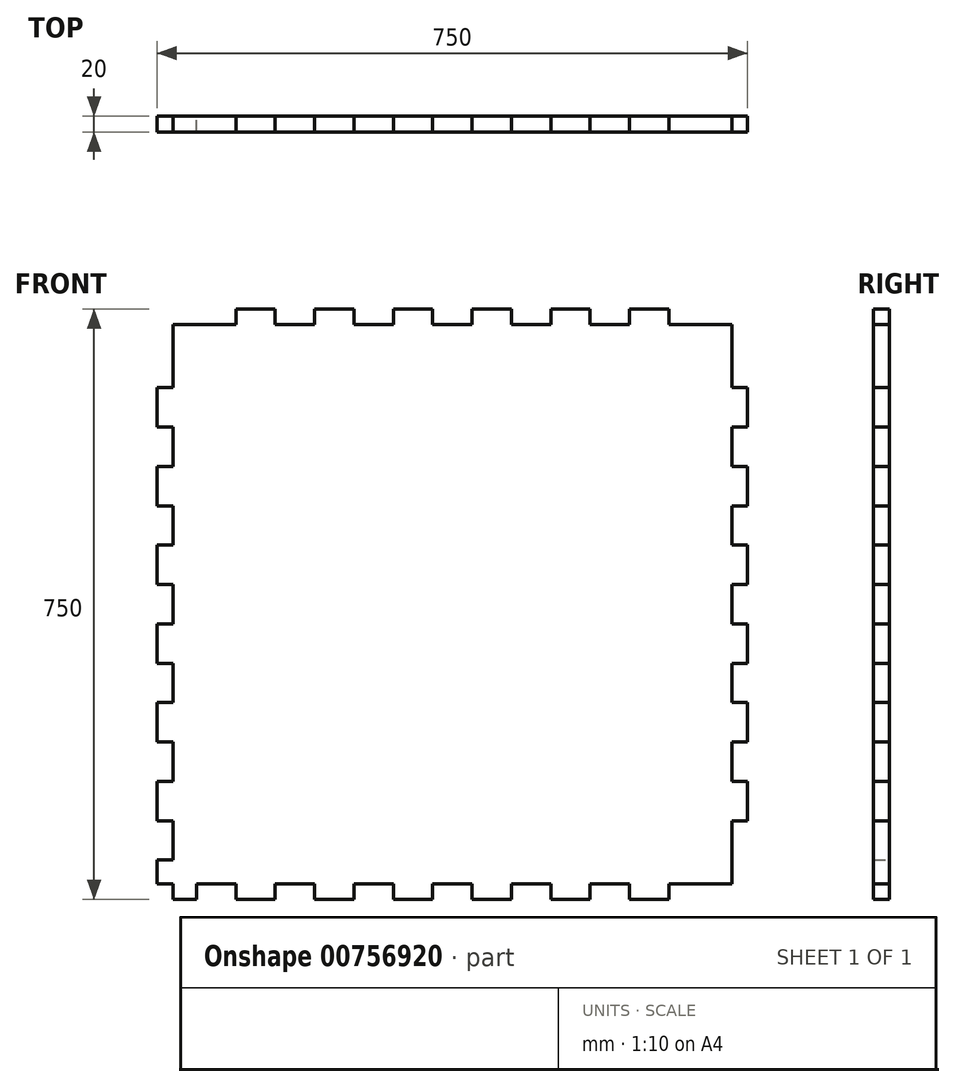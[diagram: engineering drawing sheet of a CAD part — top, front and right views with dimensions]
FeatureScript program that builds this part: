
annotation { "Feature Type Name" : "Feature", "Feature Type Description" : "" }
export const myFeature = defineFeature(function(context is Context, id is Id, definition is map)
    precondition{}
    {
        {
            var Q0;
            Q0=qCreatedBy(makeId("Front.planeOp"),FACE);
            var sketch = newSketch(context, id + "F0", { "sketchPlane" : qUnion([Q0])});
            skLineSegment(sketch, "E0.bottom", {"start": v(-346.83, 400) * mm, "end": v(403.17, 400) * mm});
            skLineSegment(sketch, "E0.top", {"start": v(-346.83, -350) * mm, "end": v(403.17, -350) * mm});
            skLineSegment(sketch, "E0.left", {"start": v(-346.83, 400) * mm, "end": v(-346.83, -350) * mm});
            skLineSegment(sketch, "E0.right", {"start": v(403.17, 400) * mm, "end": v(403.17, -350) * mm});
            skLineSegment(sketch, "E1.bottom", {"start": v(-346.83, 400) * mm, "end": v(-326.83, 400) * mm});
            skLineSegment(sketch, "E1.top", {"start": v(-346.83, 350) * mm, "end": v(-326.83, 350) * mm});
            skLineSegment(sketch, "E1.left", {"start": v(-346.83, 400) * mm, "end": v(-346.83, 350) * mm});
            skLineSegment(sketch, "E1.right", {"start": v(-326.83, 400) * mm, "end": v(-326.83, 350) * mm});
            skLineSegment(sketch, "E2.top", {"start": v(-346.83, 300) * mm, "end": v(-326.83, 300) * mm});
            skLineSegment(sketch, "E2.left", {"start": v(-346.83, 350) * mm, "end": v(-346.83, 300) * mm});
            skLineSegment(sketch, "E2.right", {"start": v(-326.83, 350) * mm, "end": v(-326.83, 300) * mm});
            skLineSegment(sketch, "E3.top", {"start": v(-346.83, 250) * mm, "end": v(-326.83, 250) * mm});
            skLineSegment(sketch, "E3.left", {"start": v(-346.83, 300) * mm, "end": v(-346.83, 250) * mm});
            skLineSegment(sketch, "E3.right", {"start": v(-326.83, 300) * mm, "end": v(-326.83, 250) * mm});
            skLineSegment(sketch, "E4.top", {"start": v(-346.83, 200) * mm, "end": v(-326.83, 200) * mm});
            skLineSegment(sketch, "E4.left", {"start": v(-346.83, 250) * mm, "end": v(-346.83, 200) * mm});
            skLineSegment(sketch, "E4.right", {"start": v(-326.83, 250) * mm, "end": v(-326.83, 200) * mm});
            skLineSegment(sketch, "E5.top", {"start": v(-346.83, 150) * mm, "end": v(-326.83, 150) * mm});
            skLineSegment(sketch, "E5.left", {"start": v(-346.83, 200) * mm, "end": v(-346.83, 150) * mm});
            skLineSegment(sketch, "E5.right", {"start": v(-326.83, 200) * mm, "end": v(-326.83, 150) * mm});
            skLineSegment(sketch, "E6.top", {"start": v(-346.83, 100) * mm, "end": v(-326.83, 100) * mm});
            skLineSegment(sketch, "E6.left", {"start": v(-346.83, 150) * mm, "end": v(-346.83, 100) * mm});
            skLineSegment(sketch, "E6.right", {"start": v(-326.83, 150) * mm, "end": v(-326.83, 100) * mm});
            skLineSegment(sketch, "E7.top", {"start": v(-346.83, 50) * mm, "end": v(-326.83, 50) * mm});
            skLineSegment(sketch, "E7.left", {"start": v(-346.83, 100) * mm, "end": v(-346.83, 50) * mm});
            skLineSegment(sketch, "E7.right", {"start": v(-326.83, 100) * mm, "end": v(-326.83, 50) * mm});
            skLineSegment(sketch, "E8.top", {"start": v(-346.83, 0) * mm, "end": v(-326.83, 0) * mm});
            skLineSegment(sketch, "E8.left", {"start": v(-346.83, 50) * mm, "end": v(-346.83, 0) * mm});
            skLineSegment(sketch, "E8.right", {"start": v(-326.83, 50) * mm, "end": v(-326.83, 0) * mm});
            skLineSegment(sketch, "E9.top", {"start": v(-346.83, -50) * mm, "end": v(-326.83, -50) * mm});
            skLineSegment(sketch, "E9.left", {"start": v(-346.83, 0) * mm, "end": v(-346.83, -50) * mm});
            skLineSegment(sketch, "E9.right", {"start": v(-326.83, 0) * mm, "end": v(-326.83, -50) * mm});
            skLineSegment(sketch, "E10.top", {"start": v(-346.83, -100) * mm, "end": v(-326.83, -100) * mm});
            skLineSegment(sketch, "E10.left", {"start": v(-346.83, -50) * mm, "end": v(-346.83, -100) * mm});
            skLineSegment(sketch, "E10.right", {"start": v(-326.83, -50) * mm, "end": v(-326.83, -100) * mm});
            skLineSegment(sketch, "E11.top", {"start": v(-346.83, -150) * mm, "end": v(-326.83, -150) * mm});
            skLineSegment(sketch, "E11.left", {"start": v(-346.83, -100) * mm, "end": v(-346.83, -150) * mm});
            skLineSegment(sketch, "E11.right", {"start": v(-326.83, -100) * mm, "end": v(-326.83, -150) * mm});
            skLineSegment(sketch, "E12.top", {"start": v(-346.83, -200) * mm, "end": v(-326.83, -200) * mm});
            skLineSegment(sketch, "E12.left", {"start": v(-346.83, -150) * mm, "end": v(-346.83, -200) * mm});
            skLineSegment(sketch, "E12.right", {"start": v(-326.83, -150) * mm, "end": v(-326.83, -200) * mm});
            skLineSegment(sketch, "E13.top", {"start": v(-346.83, -250) * mm, "end": v(-326.83, -250) * mm});
            skLineSegment(sketch, "E13.left", {"start": v(-346.83, -200) * mm, "end": v(-346.83, -250) * mm});
            skLineSegment(sketch, "E13.right", {"start": v(-326.83, -200) * mm, "end": v(-326.83, -250) * mm});
            skLineSegment(sketch, "E14.top", {"start": v(-346.83, -300) * mm, "end": v(-326.83, -300) * mm});
            skLineSegment(sketch, "E14.left", {"start": v(-346.83, -250) * mm, "end": v(-346.83, -300) * mm});
            skLineSegment(sketch, "E14.right", {"start": v(-326.83, -250) * mm, "end": v(-326.83, -300) * mm});
            skLineSegment(sketch, "E15.top", {"start": v(-346.83, -350) * mm, "end": v(-326.83, -350) * mm});
            skLineSegment(sketch, "E15.left", {"start": v(-346.83, -300) * mm, "end": v(-346.83, -350) * mm});
            skLineSegment(sketch, "E15.right", {"start": v(-326.83, -300) * mm, "end": v(-326.83, -350) * mm});
            skLineSegment(sketch, "E16.bottom", {"start": v(-346.83, -350) * mm, "end": v(-296.83, -350) * mm});
            skLineSegment(sketch, "E16.top", {"start": v(-346.83, -330) * mm, "end": v(-296.83, -330) * mm});
            skLineSegment(sketch, "E16.left", {"start": v(-346.83, -350) * mm, "end": v(-346.83, -330) * mm});
            skLineSegment(sketch, "E16.right", {"start": v(-296.83, -350) * mm, "end": v(-296.83, -330) * mm});
            skLineSegment(sketch, "E17.bottom", {"start": v(-296.83, -350) * mm, "end": v(-246.83, -350) * mm});
            skLineSegment(sketch, "E17.top", {"start": v(-296.83, -330) * mm, "end": v(-246.83, -330) * mm});
            skLineSegment(sketch, "E17.right", {"start": v(-246.83, -350) * mm, "end": v(-246.83, -330) * mm});
            skLineSegment(sketch, "E18.bottom", {"start": v(-246.83, -330) * mm, "end": v(-196.83, -330) * mm});
            skLineSegment(sketch, "E18.top", {"start": v(-246.83, -350) * mm, "end": v(-196.83, -350) * mm});
            skLineSegment(sketch, "E18.left", {"start": v(-246.83, -330) * mm, "end": v(-246.83, -350) * mm});
            skLineSegment(sketch, "E18.right", {"start": v(-196.83, -330) * mm, "end": v(-196.83, -350) * mm});
            skLineSegment(sketch, "E19.bottom", {"start": v(-196.83, -330) * mm, "end": v(-146.83, -330) * mm});
            skLineSegment(sketch, "E19.top", {"start": v(-196.83, -350) * mm, "end": v(-146.83, -350) * mm});
            skLineSegment(sketch, "E19.right", {"start": v(-146.83, -330) * mm, "end": v(-146.83, -350) * mm});
            skLineSegment(sketch, "E20.bottom", {"start": v(-146.83, -330) * mm, "end": v(-96.83, -330) * mm});
            skLineSegment(sketch, "E20.top", {"start": v(-146.83, -350) * mm, "end": v(-96.83, -350) * mm});
            skLineSegment(sketch, "E20.right", {"start": v(-96.83, -330) * mm, "end": v(-96.83, -350) * mm});
            skLineSegment(sketch, "E21.bottom", {"start": v(-96.83, -330) * mm, "end": v(-46.83, -330) * mm});
            skLineSegment(sketch, "E21.top", {"start": v(-96.83, -350) * mm, "end": v(-46.83, -350) * mm});
            skLineSegment(sketch, "E21.right", {"start": v(-46.83, -330) * mm, "end": v(-46.83, -350) * mm});
            skLineSegment(sketch, "E22.bottom", {"start": v(-46.83, -330) * mm, "end": v(3.17, -330) * mm});
            skLineSegment(sketch, "E22.top", {"start": v(-46.83, -350) * mm, "end": v(3.17, -350) * mm});
            skLineSegment(sketch, "E22.right", {"start": v(3.17, -330) * mm, "end": v(3.17, -350) * mm});
            skLineSegment(sketch, "E23.bottom", {"start": v(3.17, -330) * mm, "end": v(53.17, -330) * mm});
            skLineSegment(sketch, "E23.top", {"start": v(3.17, -350) * mm, "end": v(53.17, -350) * mm});
            skLineSegment(sketch, "E23.right", {"start": v(53.17, -330) * mm, "end": v(53.17, -350) * mm});
            skLineSegment(sketch, "E24.bottom", {"start": v(53.17, -330) * mm, "end": v(103.17, -330) * mm});
            skLineSegment(sketch, "E24.top", {"start": v(53.17, -350) * mm, "end": v(103.17, -350) * mm});
            skLineSegment(sketch, "E24.right", {"start": v(103.17, -330) * mm, "end": v(103.17, -350) * mm});
            skLineSegment(sketch, "E25.bottom", {"start": v(103.17, -330) * mm, "end": v(153.17, -330) * mm});
            skLineSegment(sketch, "E25.top", {"start": v(103.17, -350) * mm, "end": v(153.17, -350) * mm});
            skLineSegment(sketch, "E25.right", {"start": v(153.17, -330) * mm, "end": v(153.17, -350) * mm});
            skLineSegment(sketch, "E26.bottom", {"start": v(153.17, -330) * mm, "end": v(203.17, -330) * mm});
            skLineSegment(sketch, "E26.top", {"start": v(153.17, -350) * mm, "end": v(203.17, -350) * mm});
            skLineSegment(sketch, "E26.right", {"start": v(203.17, -330) * mm, "end": v(203.17, -350) * mm});
            skLineSegment(sketch, "E27.bottom", {"start": v(203.17, -330) * mm, "end": v(253.17, -330) * mm});
            skLineSegment(sketch, "E27.top", {"start": v(203.17, -350) * mm, "end": v(253.17, -350) * mm});
            skLineSegment(sketch, "E27.right", {"start": v(253.17, -330) * mm, "end": v(253.17, -350) * mm});
            skLineSegment(sketch, "E28.bottom", {"start": v(253.17, -330) * mm, "end": v(303.17, -330) * mm});
            skLineSegment(sketch, "E28.top", {"start": v(253.17, -350) * mm, "end": v(303.17, -350) * mm});
            skLineSegment(sketch, "E28.right", {"start": v(303.17, -330) * mm, "end": v(303.17, -350) * mm});
            skLineSegment(sketch, "E29.bottom", {"start": v(303.17, -330) * mm, "end": v(353.17, -330) * mm});
            skLineSegment(sketch, "E29.top", {"start": v(303.17, -350) * mm, "end": v(353.17, -350) * mm});
            skLineSegment(sketch, "E29.right", {"start": v(353.17, -330) * mm, "end": v(353.17, -350) * mm});
            skLineSegment(sketch, "E30.bottom", {"start": v(353.17, -330) * mm, "end": v(403.17, -330) * mm});
            skLineSegment(sketch, "E30.top", {"start": v(353.17, -350) * mm, "end": v(403.17, -350) * mm});
            skLineSegment(sketch, "E30.right", {"start": v(403.17, -330) * mm, "end": v(403.17, -350) * mm});
            skLineSegment(sketch, "E31.bottom", {"start": v(-346.83, 400) * mm, "end": v(-296.83, 400) * mm});
            skLineSegment(sketch, "E31.top", {"start": v(-346.83, 380) * mm, "end": v(-296.83, 380) * mm});
            skLineSegment(sketch, "E31.left", {"start": v(-346.83, 400) * mm, "end": v(-346.83, 380) * mm});
            skLineSegment(sketch, "E31.right", {"start": v(-296.83, 400) * mm, "end": v(-296.83, 380) * mm});
            skLineSegment(sketch, "E32.bottom", {"start": v(-296.83, 380) * mm, "end": v(-246.83, 380) * mm});
            skLineSegment(sketch, "E32.top", {"start": v(-296.83, 400) * mm, "end": v(-246.83, 400) * mm});
            skLineSegment(sketch, "E32.left", {"start": v(-296.83, 380) * mm, "end": v(-296.83, 400) * mm});
            skLineSegment(sketch, "E32.right", {"start": v(-246.83, 380) * mm, "end": v(-246.83, 400) * mm});
            skLineSegment(sketch, "E33.bottom", {"start": v(-246.83, 380) * mm, "end": v(-196.83, 380) * mm});
            skLineSegment(sketch, "E33.top", {"start": v(-246.83, 400) * mm, "end": v(-196.83, 400) * mm});
            skLineSegment(sketch, "E33.right", {"start": v(-196.83, 380) * mm, "end": v(-196.83, 400) * mm});
            skLineSegment(sketch, "E34.bottom", {"start": v(-196.83, 380) * mm, "end": v(-146.83, 380) * mm});
            skLineSegment(sketch, "E34.top", {"start": v(-196.83, 400) * mm, "end": v(-146.83, 400) * mm});
            skLineSegment(sketch, "E34.right", {"start": v(-146.83, 380) * mm, "end": v(-146.83, 400) * mm});
            skLineSegment(sketch, "E35.bottom", {"start": v(-146.83, 380) * mm, "end": v(-96.83, 380) * mm});
            skLineSegment(sketch, "E35.top", {"start": v(-146.83, 400) * mm, "end": v(-96.83, 400) * mm});
            skLineSegment(sketch, "E35.right", {"start": v(-96.83, 380) * mm, "end": v(-96.83, 400) * mm});
            skLineSegment(sketch, "E36.bottom", {"start": v(-96.83, 380) * mm, "end": v(-46.83, 380) * mm});
            skLineSegment(sketch, "E36.top", {"start": v(-96.83, 400) * mm, "end": v(-46.83, 400) * mm});
            skLineSegment(sketch, "E36.right", {"start": v(-46.83, 380) * mm, "end": v(-46.83, 400) * mm});
            skLineSegment(sketch, "E37.bottom", {"start": v(-46.83, 380) * mm, "end": v(3.17, 380) * mm});
            skLineSegment(sketch, "E37.top", {"start": v(-46.83, 400) * mm, "end": v(3.17, 400) * mm});
            skLineSegment(sketch, "E37.right", {"start": v(3.17, 380) * mm, "end": v(3.17, 400) * mm});
            skLineSegment(sketch, "E38.bottom", {"start": v(3.17, 380) * mm, "end": v(53.17, 380) * mm});
            skLineSegment(sketch, "E38.top", {"start": v(3.17, 400) * mm, "end": v(53.17, 400) * mm});
            skLineSegment(sketch, "E38.right", {"start": v(53.17, 380) * mm, "end": v(53.17, 400) * mm});
            skLineSegment(sketch, "E39.bottom", {"start": v(53.17, 380) * mm, "end": v(103.17, 380) * mm});
            skLineSegment(sketch, "E39.top", {"start": v(53.17, 400) * mm, "end": v(103.17, 400) * mm});
            skLineSegment(sketch, "E39.right", {"start": v(103.17, 380) * mm, "end": v(103.17, 400) * mm});
            skLineSegment(sketch, "E40.bottom", {"start": v(103.17, 380) * mm, "end": v(153.17, 380) * mm});
            skLineSegment(sketch, "E40.top", {"start": v(103.17, 400) * mm, "end": v(153.17, 400) * mm});
            skLineSegment(sketch, "E40.right", {"start": v(153.17, 380) * mm, "end": v(153.17, 400) * mm});
            skLineSegment(sketch, "E41.bottom", {"start": v(153.17, 380) * mm, "end": v(203.17, 380) * mm});
            skLineSegment(sketch, "E41.top", {"start": v(153.17, 400) * mm, "end": v(203.17, 400) * mm});
            skLineSegment(sketch, "E41.right", {"start": v(203.17, 380) * mm, "end": v(203.17, 400) * mm});
            skLineSegment(sketch, "E42.bottom", {"start": v(203.17, 380) * mm, "end": v(253.17, 380) * mm});
            skLineSegment(sketch, "E42.top", {"start": v(203.17, 400) * mm, "end": v(253.17, 400) * mm});
            skLineSegment(sketch, "E42.right", {"start": v(253.17, 380) * mm, "end": v(253.17, 400) * mm});
            skLineSegment(sketch, "E43.bottom", {"start": v(253.17, 380) * mm, "end": v(303.17, 380) * mm});
            skLineSegment(sketch, "E43.top", {"start": v(253.17, 400) * mm, "end": v(303.17, 400) * mm});
            skLineSegment(sketch, "E43.right", {"start": v(303.17, 380) * mm, "end": v(303.17, 400) * mm});
            skLineSegment(sketch, "E44.bottom", {"start": v(303.17, 380) * mm, "end": v(353.17, 380) * mm});
            skLineSegment(sketch, "E44.top", {"start": v(303.17, 400) * mm, "end": v(353.17, 400) * mm});
            skLineSegment(sketch, "E44.right", {"start": v(353.17, 380) * mm, "end": v(353.17, 400) * mm});
            skLineSegment(sketch, "E45.bottom", {"start": v(353.17, 380) * mm, "end": v(403.17, 380) * mm});
            skLineSegment(sketch, "E45.top", {"start": v(353.17, 400) * mm, "end": v(403.17, 400) * mm});
            skLineSegment(sketch, "E45.right", {"start": v(403.17, 380) * mm, "end": v(403.17, 400) * mm});
            skLineSegment(sketch, "E46.bottom", {"start": v(403.17, 400) * mm, "end": v(383.17, 400) * mm});
            skLineSegment(sketch, "E46.top", {"start": v(403.17, 350) * mm, "end": v(383.17, 350) * mm});
            skLineSegment(sketch, "E46.left", {"start": v(403.17, 400) * mm, "end": v(403.17, 350) * mm});
            skLineSegment(sketch, "E46.right", {"start": v(383.17, 400) * mm, "end": v(383.17, 350) * mm});
            skLineSegment(sketch, "E47.bottom", {"start": v(383.17, 350) * mm, "end": v(403.17, 350) * mm});
            skLineSegment(sketch, "E47.top", {"start": v(383.17, 300) * mm, "end": v(403.17, 300) * mm});
            skLineSegment(sketch, "E47.left", {"start": v(383.17, 350) * mm, "end": v(383.17, 300) * mm});
            skLineSegment(sketch, "E47.right", {"start": v(403.17, 350) * mm, "end": v(403.17, 300) * mm});
            skLineSegment(sketch, "E48.top", {"start": v(383.17, 250) * mm, "end": v(403.17, 250) * mm});
            skLineSegment(sketch, "E48.left", {"start": v(383.17, 300) * mm, "end": v(383.17, 250) * mm});
            skLineSegment(sketch, "E48.right", {"start": v(403.17, 300) * mm, "end": v(403.17, 250) * mm});
            skLineSegment(sketch, "E49.top", {"start": v(383.17, 200) * mm, "end": v(403.17, 200) * mm});
            skLineSegment(sketch, "E49.left", {"start": v(383.17, 250) * mm, "end": v(383.17, 200) * mm});
            skLineSegment(sketch, "E49.right", {"start": v(403.17, 250) * mm, "end": v(403.17, 200) * mm});
            skLineSegment(sketch, "E50.top", {"start": v(383.17, 150) * mm, "end": v(403.17, 150) * mm});
            skLineSegment(sketch, "E50.left", {"start": v(383.17, 200) * mm, "end": v(383.17, 150) * mm});
            skLineSegment(sketch, "E50.right", {"start": v(403.17, 200) * mm, "end": v(403.17, 150) * mm});
            skLineSegment(sketch, "E51.top", {"start": v(383.17, 100) * mm, "end": v(403.17, 100) * mm});
            skLineSegment(sketch, "E51.left", {"start": v(383.17, 150) * mm, "end": v(383.17, 100) * mm});
            skLineSegment(sketch, "E51.right", {"start": v(403.17, 150) * mm, "end": v(403.17, 100) * mm});
            skLineSegment(sketch, "E52.top", {"start": v(383.17, 50) * mm, "end": v(403.17, 50) * mm});
            skLineSegment(sketch, "E52.left", {"start": v(383.17, 100) * mm, "end": v(383.17, 50) * mm});
            skLineSegment(sketch, "E52.right", {"start": v(403.17, 100) * mm, "end": v(403.17, 50) * mm});
            skLineSegment(sketch, "E53.top", {"start": v(383.17, 0) * mm, "end": v(403.17, 0) * mm});
            skLineSegment(sketch, "E53.left", {"start": v(383.17, 50) * mm, "end": v(383.17, 0) * mm});
            skLineSegment(sketch, "E53.right", {"start": v(403.17, 50) * mm, "end": v(403.17, 0) * mm});
            skLineSegment(sketch, "E54.top", {"start": v(383.17, -50) * mm, "end": v(403.17, -50) * mm});
            skLineSegment(sketch, "E54.left", {"start": v(383.17, 0) * mm, "end": v(383.17, -50) * mm});
            skLineSegment(sketch, "E54.right", {"start": v(403.17, 0) * mm, "end": v(403.17, -50) * mm});
            skLineSegment(sketch, "E55.top", {"start": v(383.17, -100) * mm, "end": v(403.17, -100) * mm});
            skLineSegment(sketch, "E55.left", {"start": v(383.17, -50) * mm, "end": v(383.17, -100) * mm});
            skLineSegment(sketch, "E55.right", {"start": v(403.17, -50) * mm, "end": v(403.17, -100) * mm});
            skLineSegment(sketch, "E56.top", {"start": v(383.17, -150) * mm, "end": v(403.17, -150) * mm});
            skLineSegment(sketch, "E56.left", {"start": v(383.17, -100) * mm, "end": v(383.17, -150) * mm});
            skLineSegment(sketch, "E56.right", {"start": v(403.17, -100) * mm, "end": v(403.17, -150) * mm});
            skLineSegment(sketch, "E57.top", {"start": v(383.17, -200) * mm, "end": v(403.17, -200) * mm});
            skLineSegment(sketch, "E57.left", {"start": v(383.17, -150) * mm, "end": v(383.17, -200) * mm});
            skLineSegment(sketch, "E57.right", {"start": v(403.17, -150) * mm, "end": v(403.17, -200) * mm});
            skLineSegment(sketch, "E58.top", {"start": v(383.17, -250) * mm, "end": v(403.17, -250) * mm});
            skLineSegment(sketch, "E58.left", {"start": v(383.17, -200) * mm, "end": v(383.17, -250) * mm});
            skLineSegment(sketch, "E58.right", {"start": v(403.17, -200) * mm, "end": v(403.17, -250) * mm});
            skLineSegment(sketch, "E59.top", {"start": v(383.17, -300) * mm, "end": v(403.17, -300) * mm});
            skLineSegment(sketch, "E59.left", {"start": v(383.17, -250) * mm, "end": v(383.17, -300) * mm});
            skLineSegment(sketch, "E59.right", {"start": v(403.17, -250) * mm, "end": v(403.17, -300) * mm});
            skLineSegment(sketch, "E60.top", {"start": v(383.17, -350) * mm, "end": v(403.17, -350) * mm});
            skLineSegment(sketch, "E60.left", {"start": v(383.17, -300) * mm, "end": v(383.17, -350) * mm});
            skLineSegment(sketch, "E60.right", {"start": v(403.17, -300) * mm, "end": v(403.17, -350) * mm});
            skSolve(sketch);
        }
        {
            var Q0;
            {var subQ5=sQuery(id+"F0.wireOp",EDGE,"E31.left");Q0=makeQuery(id+"F0.imprint","IMPRINT",FACE,{"disambiguationData":[TD([[makeQuery(id+"F0.imprint","IMPRINT",EDGE,{"derivedFrom":subQ5}),1.0]])]});}
            var Q1;
            {var subQ0=sQuery(id+"F0.wireOp",EDGE,"E1.left");Q1=makeQuery(id+"F0.imprint","IMPRINT",FACE,{"disambiguationData":[TD([[makeQuery(id+"F0.imprint","IMPRINT",EDGE,{"derivedFrom":subQ0}),1.0]])]});}
            var Q2;
            {var subQ5=sQuery(id+"F0.wireOp",EDGE,"E32.left");Q2=makeQuery(id+"F0.imprint","IMPRINT",FACE,{"disambiguationData":[TD([[makeQuery(id+"F0.imprint","IMPRINT",EDGE,{"derivedFrom":subQ5}),1.0]])]});}
            var Q3;
            Q3=makeQuery(id+"F0.imprint","IMPRINT",FACE,{"disambiguationData":[TD([[makeQuery(id+"F0.imprint","IMPRINT",EDGE,{"derivedFrom":sQuery(id+"F0.wireOp",EDGE,"E33.bottom")}),1.0]])]});
            var Q4;
            Q4=makeQuery(id+"F0.imprint","IMPRINT",FACE,{"disambiguationData":[TD([[makeQuery(id+"F0.imprint","IMPRINT",EDGE,{"derivedFrom":sQuery(id+"F0.wireOp",EDGE,"E35.bottom")}),1.0]])]});
            var Q5;
            Q5=makeQuery(id+"F0.imprint","IMPRINT",FACE,{"disambiguationData":[TD([[makeQuery(id+"F0.imprint","IMPRINT",EDGE,{"derivedFrom":sQuery(id+"F0.wireOp",EDGE,"E37.bottom")}),1.0]])]});
            var Q6;
            Q6=makeQuery(id+"F0.imprint","IMPRINT",FACE,{"disambiguationData":[TD([[makeQuery(id+"F0.imprint","IMPRINT",EDGE,{"derivedFrom":sQuery(id+"F0.wireOp",EDGE,"E39.bottom")}),1.0]])]});
            var Q7;
            Q7=makeQuery(id+"F0.imprint","IMPRINT",FACE,{"disambiguationData":[TD([[makeQuery(id+"F0.imprint","IMPRINT",EDGE,{"derivedFrom":sQuery(id+"F0.wireOp",EDGE,"E41.bottom")}),1.0]])]});
            var Q8;
            Q8=makeQuery(id+"F0.imprint","IMPRINT",FACE,{"disambiguationData":[TD([[makeQuery(id+"F0.imprint","IMPRINT",EDGE,{"derivedFrom":sQuery(id+"F0.wireOp",EDGE,"E43.bottom")}),1.0]])]});
            var Q9;
            {var subQ4=sQuery(id+"F0.wireOp",EDGE,"E45.top");Q9=makeQuery(id+"F0.imprint","IMPRINT",FACE,{"disambiguationData":[TD([[makeQuery(id+"F0.imprint","IMPRINT",EDGE,{"derivedFrom":subQ4}),-1.0]])]});}
            var Q10;
            {var subQ5=sQuery(id+"F0.wireOp",EDGE,"E46.bottom");Q10=makeQuery(id+"F0.imprint","IMPRINT",FACE,{"disambiguationData":[TD([[makeQuery(id+"F0.imprint","IMPRINT",EDGE,{"derivedFrom":subQ5}),1.0]])]});}
            var Q11;
            {var subQ5=sQuery(id+"F0.wireOp",EDGE,"E47.bottom");Q11=makeQuery(id+"F0.imprint","IMPRINT",FACE,{"disambiguationData":[TD([[makeQuery(id+"F0.imprint","IMPRINT",EDGE,{"derivedFrom":subQ5}),1.0]])]});}
            var Q12;
            Q12=makeQuery(id+"F0.imprint","IMPRINT",FACE,{"disambiguationData":[TD([[makeQuery(id+"F0.imprint","IMPRINT",EDGE,{"derivedFrom":sQuery(id+"F0.wireOp",EDGE,"E2.top")}),-1.0]])]});
            var Q13;
            Q13=makeQuery(id+"F0.imprint","IMPRINT",FACE,{"disambiguationData":[TD([[makeQuery(id+"F0.imprint","IMPRINT",EDGE,{"derivedFrom":sQuery(id+"F0.wireOp",EDGE,"E4.top")}),-1.0]])]});
            var Q14;
            Q14=makeQuery(id+"F0.imprint","IMPRINT",FACE,{"disambiguationData":[TD([[makeQuery(id+"F0.imprint","IMPRINT",EDGE,{"derivedFrom":sQuery(id+"F0.wireOp",EDGE,"E6.top")}),-1.0]])]});
            var Q15;
            Q15=makeQuery(id+"F0.imprint","IMPRINT",FACE,{"disambiguationData":[TD([[makeQuery(id+"F0.imprint","IMPRINT",EDGE,{"derivedFrom":sQuery(id+"F0.wireOp",EDGE,"E8.top")}),-1.0]])]});
            var Q16;
            Q16=makeQuery(id+"F0.imprint","IMPRINT",FACE,{"disambiguationData":[TD([[makeQuery(id+"F0.imprint","IMPRINT",EDGE,{"derivedFrom":sQuery(id+"F0.wireOp",EDGE,"E10.top")}),-1.0]])]});
            var Q17;
            Q17=makeQuery(id+"F0.imprint","IMPRINT",FACE,{"disambiguationData":[TD([[makeQuery(id+"F0.imprint","IMPRINT",EDGE,{"derivedFrom":sQuery(id+"F0.wireOp",EDGE,"E12.top")}),-1.0]])]});
            var Q18;
            {var subQ0=sQuery(id+"F0.wireOp",EDGE,"E14.top");Q18=makeQuery(id+"F0.imprint","IMPRINT",FACE,{"disambiguationData":[TD([[makeQuery(id+"F0.imprint","IMPRINT",EDGE,{"derivedFrom":subQ0}),-1.0]])]});}
            var Q19;
            {var subQ5=sQuery(id+"F0.wireOp",EDGE,"E16.left");Q19=makeQuery(id+"F0.imprint","IMPRINT",FACE,{"disambiguationData":[TD([[makeQuery(id+"F0.imprint","IMPRINT",EDGE,{"derivedFrom":subQ5}),-1.0]])]});}
            var Q20;
            {var subQ5=sQuery(id+"F0.wireOp",EDGE,"E16.right");Q20=makeQuery(id+"F0.imprint","IMPRINT",FACE,{"disambiguationData":[TD([[makeQuery(id+"F0.imprint","IMPRINT",EDGE,{"derivedFrom":subQ5}),1.0]])]});}
            var Q21;
            Q21=makeQuery(id+"F0.imprint","IMPRINT",FACE,{"disambiguationData":[TD([[makeQuery(id+"F0.imprint","IMPRINT",EDGE,{"derivedFrom":sQuery(id+"F0.wireOp",EDGE,"E18.bottom")}),-1.0]])]});
            var Q22;
            Q22=makeQuery(id+"F0.imprint","IMPRINT",FACE,{"disambiguationData":[TD([[makeQuery(id+"F0.imprint","IMPRINT",EDGE,{"derivedFrom":sQuery(id+"F0.wireOp",EDGE,"E20.bottom")}),-1.0]])]});
            var Q23;
            Q23=makeQuery(id+"F0.imprint","IMPRINT",FACE,{"disambiguationData":[TD([[makeQuery(id+"F0.imprint","IMPRINT",EDGE,{"derivedFrom":sQuery(id+"F0.wireOp",EDGE,"E22.bottom")}),-1.0]])]});
            var Q24;
            Q24=makeQuery(id+"F0.imprint","IMPRINT",FACE,{"disambiguationData":[TD([[makeQuery(id+"F0.imprint","IMPRINT",EDGE,{"derivedFrom":sQuery(id+"F0.wireOp",EDGE,"E24.bottom")}),-1.0]])]});
            var Q25;
            Q25=makeQuery(id+"F0.imprint","IMPRINT",FACE,{"disambiguationData":[TD([[makeQuery(id+"F0.imprint","IMPRINT",EDGE,{"derivedFrom":sQuery(id+"F0.wireOp",EDGE,"E26.bottom")}),-1.0]])]});
            var Q26;
            Q26=makeQuery(id+"F0.imprint","IMPRINT",FACE,{"disambiguationData":[TD([[makeQuery(id+"F0.imprint","IMPRINT",EDGE,{"derivedFrom":sQuery(id+"F0.wireOp",EDGE,"E28.bottom")}),-1.0]])]});
            var Q27;
            {var subQ4=sQuery(id+"F0.wireOp",EDGE,"E30.top");Q27=makeQuery(id+"F0.imprint","IMPRINT",FACE,{"disambiguationData":[TD([[makeQuery(id+"F0.imprint","IMPRINT",EDGE,{"derivedFrom":subQ4}),1.0]])]});}
            var Q28;
            {var subQ5=sQuery(id+"F0.wireOp",EDGE,"E60.top");Q28=makeQuery(id+"F0.imprint","IMPRINT",FACE,{"disambiguationData":[TD([[makeQuery(id+"F0.imprint","IMPRINT",EDGE,{"derivedFrom":subQ5}),1.0]])]});}
            var Q29;
            {var subQ5=sQuery(id+"F0.wireOp",EDGE,"E59.top");Q29=makeQuery(id+"F0.imprint","IMPRINT",FACE,{"disambiguationData":[TD([[makeQuery(id+"F0.imprint","IMPRINT",EDGE,{"derivedFrom":subQ5}),-1.0]])]});}
            var Q30;
            Q30=makeQuery(id+"F0.imprint","IMPRINT",FACE,{"disambiguationData":[TD([[makeQuery(id+"F0.imprint","IMPRINT",EDGE,{"derivedFrom":sQuery(id+"F0.wireOp",EDGE,"E57.top")}),-1.0]])]});
            var Q31;
            Q31=makeQuery(id+"F0.imprint","IMPRINT",FACE,{"disambiguationData":[TD([[makeQuery(id+"F0.imprint","IMPRINT",EDGE,{"derivedFrom":sQuery(id+"F0.wireOp",EDGE,"E55.top")}),-1.0]])]});
            var Q32;
            Q32=makeQuery(id+"F0.imprint","IMPRINT",FACE,{"disambiguationData":[TD([[makeQuery(id+"F0.imprint","IMPRINT",EDGE,{"derivedFrom":sQuery(id+"F0.wireOp",EDGE,"E53.top")}),-1.0]])]});
            var Q33;
            Q33=makeQuery(id+"F0.imprint","IMPRINT",FACE,{"disambiguationData":[TD([[makeQuery(id+"F0.imprint","IMPRINT",EDGE,{"derivedFrom":sQuery(id+"F0.wireOp",EDGE,"E51.top")}),-1.0]])]});
            var Q34;
            Q34=makeQuery(id+"F0.imprint","IMPRINT",FACE,{"disambiguationData":[TD([[makeQuery(id+"F0.imprint","IMPRINT",EDGE,{"derivedFrom":sQuery(id+"F0.wireOp",EDGE,"E49.top")}),-1.0]])]});
            var Q35;
            Q35=makeQuery(id+"F0.imprint","IMPRINT",FACE,{"disambiguationData":[TD([[makeQuery(id+"F0.imprint","IMPRINT",EDGE,{"derivedFrom":sQuery(id+"F0.wireOp",EDGE,"E47.top")}),-1.0]])]});
            var Q36;
            {var subQ17=sQuery(id+"F0.wireOp",EDGE,"E2.right");Q36=makeQuery(id+"F0.imprint","IMPRINT",FACE,{"disambiguationData":[TD([[makeQuery(id+"F0.imprint","IMPRINT",EDGE,{"derivedFrom":subQ17}),1.0]])]});}
            extrude(context, id + "F1", {"entities" : qUnion([Q0, Q1, Q2, Q3, Q4, Q5, Q6, Q7, Q8, Q9, Q10, Q11, Q12, Q13, Q14, Q15, Q16, Q17, Q18, Q19, Q20, Q21, Q22, Q23, Q24, Q25, Q26, Q27, Q28, Q29, Q30, Q31, Q32, Q33, Q34, Q35, Q36]), "depth" : 20 * mm, "offsetDistance" : 25.4 * mm});
        }
    });
